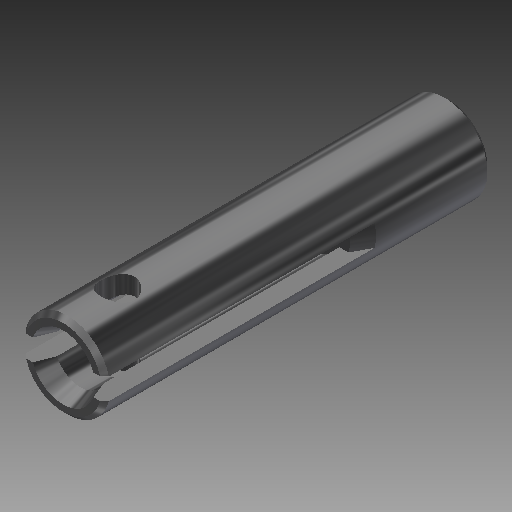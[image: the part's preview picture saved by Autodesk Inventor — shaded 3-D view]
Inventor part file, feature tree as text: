
AUTODESK INVENTOR PART (.ipt)
format: ipt  version: 2019 (Build 230136000, 136)  size: 215,040 bytes
history: native  units: mm
features: chamfer x6, sketch x4, extrude x3, other x2, hole x1
ambient origin geometry x8: Origin, YZ Plane, XZ Plane, XY Plane, X Axis, Y Axis, Z Axis, Center Point
bodies: Solid1 (feature_tree)
feature tree (16):
  extrude  "Extrusion1"  Depth=90.0mm TaperAngle=0.0deg
  extrude  "Extrusion2"  Depth=5.0mm
  chamfer  "Chamfer1"  Distance=10.0mm
  chamfer  "Chamfer2"  Distance=59.0mm
  chamfer  "Chamfer3"  Distance=1.0mm Angle=45.0deg
  chamfer  "Chamfer4"  Distance=1.5mm Angle=45.0deg
  chamfer  "Chamfer5"  Distance=1.5mm Angle=45.0deg
  chamfer  "Chamfer6"  Distance=4.0mm Angle=45.0deg
  hole  "Hole1"  [1 undecoded]
  extrude  "Extrusion3"  Depth=10.0mm TaperAngle=45.0deg
  other  "Work Point1"
  sketch  "Sketch1"  dims[d0=20.0mm d1=90.0mm d2=0.0mm]
  sketch  "Sketch2"  dims[d3=12.0mm d4=5.0mm]
  sketch  "Sketch3"  dims[d5=2.5mm]
  sketch  "Sketch4"  dims[d6=20.0mm d7=10.0mm d8=59.0mm d9=0.0mm d10=1.0mm d11=2.0mm d12=45.0deg d13=1.5mm d14=4.0mm d15=45.0deg d16=1.5mm d17=4.0mm d18=45.0deg d19=4.0mm d20=2.0mm d21=45.0deg d22=4.0mm d23=2.0mm d24=45.0deg d25=1.0mm d26=2.0mm d27=45.0deg d28=10.106mm d29=6.0mm d30=4.0mm d31=2.0mm d32=90.0deg d33=45.0mm d34=0.0mm d35=12.703mm d36=7.9mm d37=59.0mm d38=0.0mm d67=-137336.0mm d68=-4973.8mm d69=11076.2mm d70=25345.7mm d71=0.0mm d72=25077.0mm d73=-240.0mm d74=-0.0mm d75=-446103.0mm d76=7282.0mm d77=0.0mm d78=-446589.0mm d79=9810.0mm d80=0.048171mm]
  other  "Work Axis1"
note: 1 required parameter value undecoded (feature->parameter linkage not recoverable at this tier; creation-order binding heuristic only, values carry confidence <= 0.55)
